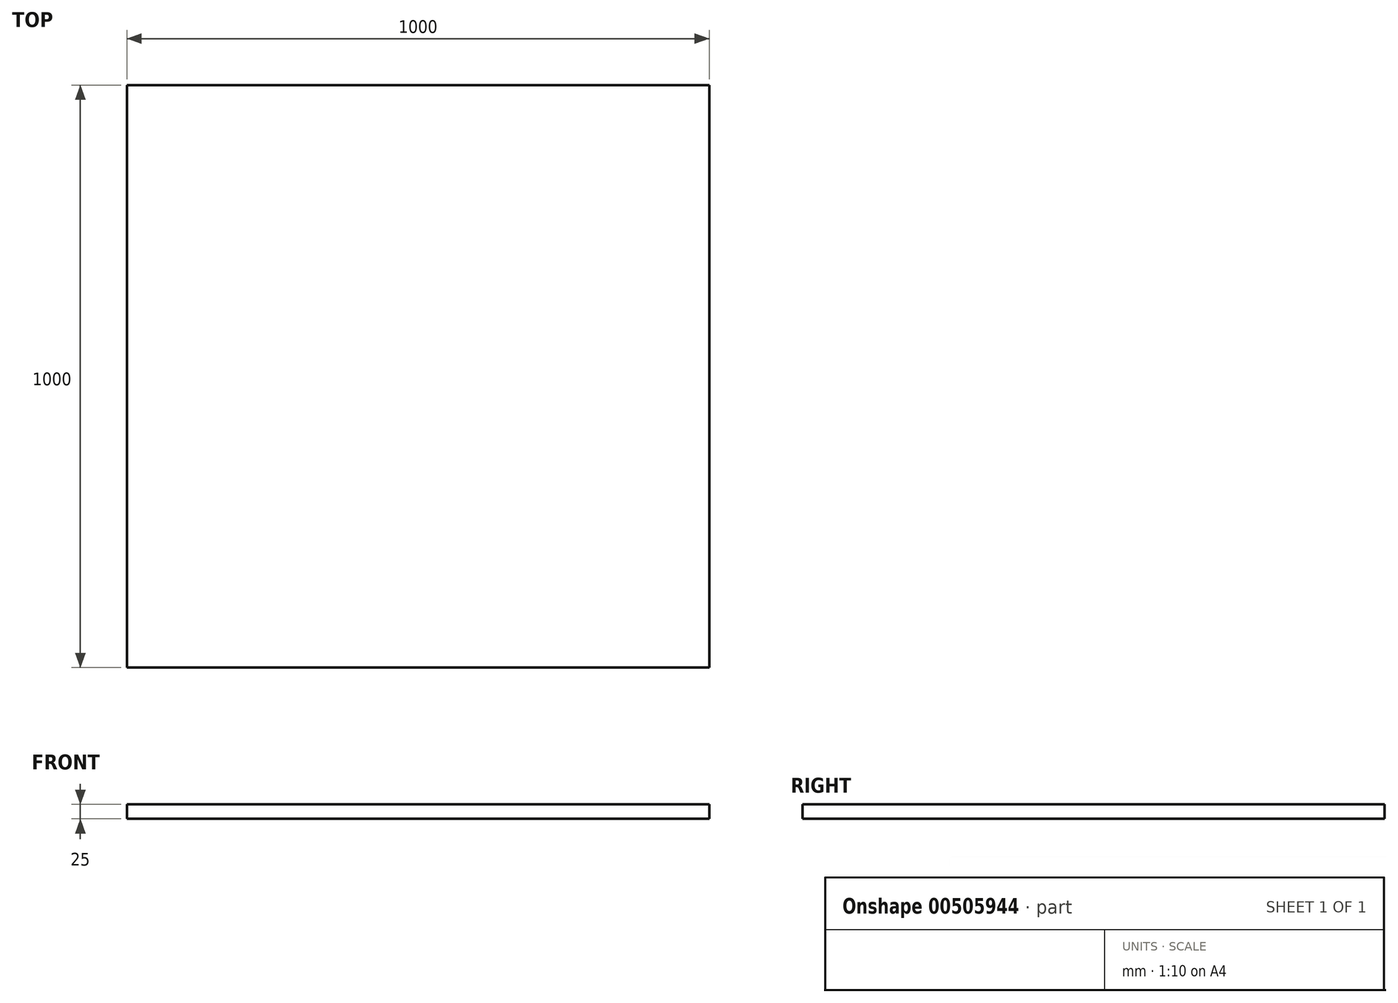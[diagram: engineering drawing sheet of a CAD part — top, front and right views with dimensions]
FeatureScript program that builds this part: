
annotation { "Feature Type Name" : "Feature", "Feature Type Description" : "" }
export const myFeature = defineFeature(function(context is Context, id is Id, definition is map)
    precondition{}
    {
        {
            var Q0;
            Q0=qCreatedBy(makeId("Top.planeOp"),FACE);
            var sketch = newSketch(context, id + "F0", { "sketchPlane" : qUnion([Q0])});
            skLineSegment(sketch, "E0.bottom", {"start": v(889.88, 914.43) * mm, "end": v(-110.12, 914.43) * mm});
            skLineSegment(sketch, "E0.top", {"start": v(889.88, -85.57) * mm, "end": v(-110.12, -85.57) * mm});
            skLineSegment(sketch, "E0.left", {"start": v(889.88, 914.43) * mm, "end": v(889.88, -85.57) * mm});
            skLineSegment(sketch, "E0.right", {"start": v(-110.12, 914.43) * mm, "end": v(-110.12, -85.57) * mm});
            skSolve(sketch);
        }
        {
            var Q0;
            Q0 = qSketchRegion(id + "F0", true);
            extrude(context, id + "F1", {"entities" : qUnion([Q0]), "depth" : 25 * mm, "offsetDistance" : 25 * mm});
        }
    });
